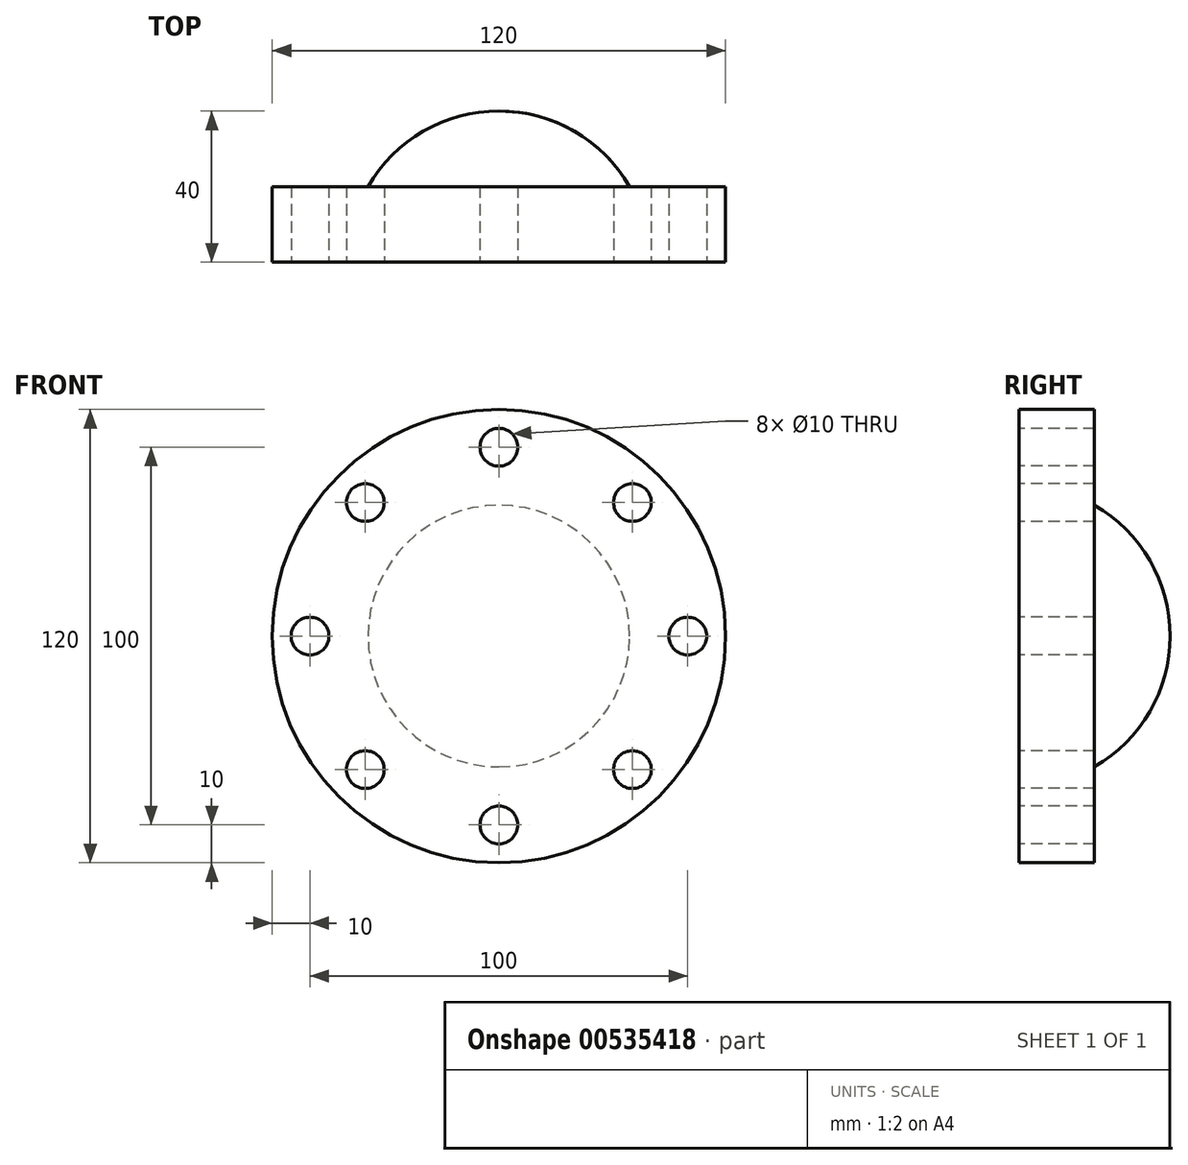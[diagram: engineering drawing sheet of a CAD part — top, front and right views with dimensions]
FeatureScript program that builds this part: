
annotation { "Feature Type Name" : "Feature", "Feature Type Description" : "" }
export const myFeature = defineFeature(function(context is Context, id is Id, definition is map)
    precondition{}
    {
        {
            var Q0;
            Q0=qCreatedBy(makeId("Front.planeOp"),FACE);
            var sketch = newSketch(context, id + "F0", { "sketchPlane" : qUnion([Q0])});
            skCircle(sketch, "E0", {"center": v(0, 0) * mm, "radius": 60 * mm});
            skCircle(sketch, "E1", {"center": v(0, 50) * mm, "radius": 5 * mm});
            skCircle(sketch, "E2.1.0", {"center": v(-35.36, 35.36) * mm, "radius": 5 * mm});
            skCircle(sketch, "E2.2.0", {"center": v(-50, 0) * mm, "radius": 5 * mm});
            skCircle(sketch, "E2.3.0", {"center": v(-35.36, -35.36) * mm, "radius": 5 * mm});
            skCircle(sketch, "E2.4.0", {"center": v(0, -50) * mm, "radius": 5 * mm});
            skCircle(sketch, "E2.5.0", {"center": v(35.36, -35.36) * mm, "radius": 5 * mm});
            skCircle(sketch, "E2.6.0", {"center": v(50, 0) * mm, "radius": 5 * mm});
            skCircle(sketch, "E2.7.0", {"center": v(35.36, 35.36) * mm, "radius": 5 * mm});
            skSolve(sketch);
        }
        {
            var Q0;
            Q0=makeQuery(id+"F0.imprint","IMPRINT",FACE,{"disambiguationData":[TD([[makeQuery(id+"F0.imprint","IMPRINT",EDGE,{"derivedFrom":sQuery(id+"F0.wireOp",EDGE,"E0")}),1.0]])]});
            extrude(context, id + "F1", {"entities" : qUnion([Q0]), "oppositeDirection" : true, "depth" : 20 * mm, "offsetDistance" : 25 * mm});
        }
        {
            var Q0;
            Q0=qCreatedBy(makeId("Top.planeOp"),FACE);
            var sketch = newSketch(context, id + "F2", { "sketchPlane" : qUnion([Q0])});
            skArc(sketch, "E3", {"start": v(0, 40) * mm, "mid": v(-20, 34.64) * mm, "end": v(-34.64, 20) * mm});
            skLineSegment(sketch, "E4", {"start": v(0, 20) * mm, "end": v(0, 40) * mm});
            skLineSegment(sketch, "E5", {"start": v(0, 20) * mm, "end": v(-34.64, 20) * mm});
            skSolve(sketch);
        }
        {
            var Q0;
            Q0=makeQuery(id+"F2.imprint","IMPRINT",FACE,{"disambiguationData":[TD([[makeQuery(id+"F2.imprint","IMPRINT",EDGE,{"derivedFrom":sQuery(id+"F2.wireOp",EDGE,"E3")}),1.0]])]});
            var Q1;
            Q1=sQuery(id+"F2.wireOp",EDGE,"E4");
            revolve(context, id + "F3", {"operationType" : NewBodyOperationType.ADD, "entities" : qUnion([Q0]), "axis" : qUnion([Q1]), "revolveType" : RevolveType.FULL});
        }
    });
